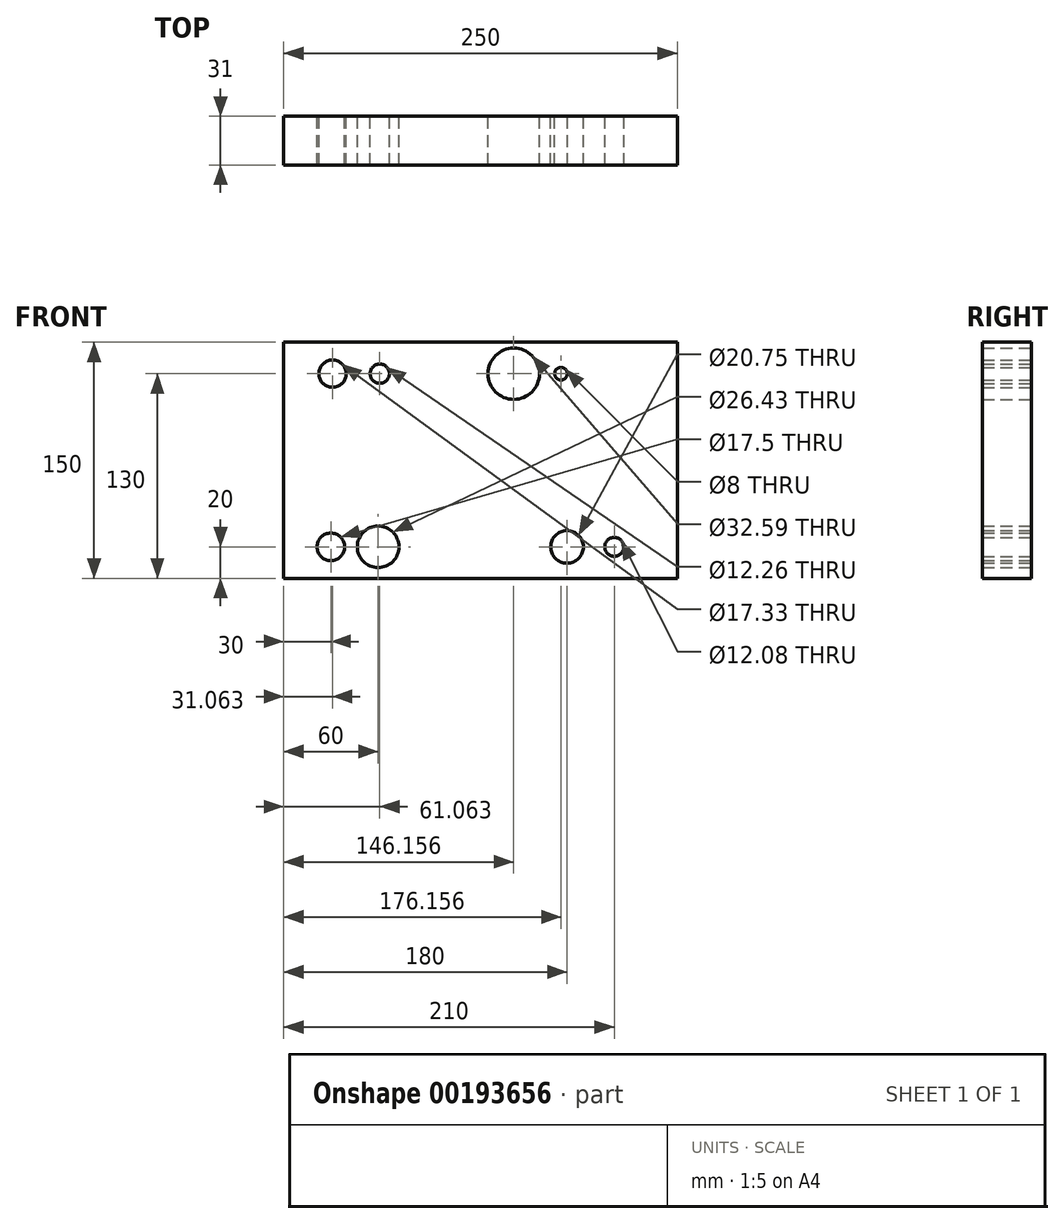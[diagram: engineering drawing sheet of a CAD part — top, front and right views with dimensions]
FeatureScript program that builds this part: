
annotation { "Feature Type Name" : "Feature", "Feature Type Description" : "" }
export const myFeature = defineFeature(function(context is Context, id is Id, definition is map)
    precondition{}
    {
        {
            var Q0;
            Q0=qCreatedBy(makeId("Front.planeOp"),FACE);
            var sketch = newSketch(context, id + "F0", { "sketchPlane" : qUnion([Q0])});
            skLineSegment(sketch, "E0.bottom", {"start": v(125, 75) * mm, "end": v(-125, 75) * mm});
            skLineSegment(sketch, "E0.top", {"start": v(125, -75) * mm, "end": v(-125, -75) * mm});
            skLineSegment(sketch, "E0.left", {"start": v(125, 75) * mm, "end": v(125, -75) * mm});
            skLineSegment(sketch, "E0.right", {"start": v(-125, 75) * mm, "end": v(-125, -75) * mm});
            skPoint(sketch, "E0.middle", {"position": v(0, 0) * mm});
            skCircle(sketch, "E1", {"center": v(-93.94, 55) * mm, "radius": 8.67 * mm});
            skCircle(sketch, "E2", {"center": v(-63.94, 55) * mm, "radius": 6.13 * mm});
            skCircle(sketch, "E3", {"center": v(21.16, 55) * mm, "radius": 16.3 * mm});
            skCircle(sketch, "E4", {"center": v(51.16, 55) * mm, "radius": 4 * mm});
            skCircle(sketch, "E5", {"center": v(-95, -55) * mm, "radius": 8.75 * mm});
            skCircle(sketch, "E6", {"center": v(-65, -55) * mm, "radius": 13.21 * mm});
            skCircle(sketch, "E7", {"center": v(55, -55) * mm, "radius": 10.37 * mm});
            skCircle(sketch, "E8", {"center": v(85, -55) * mm, "radius": 6.04 * mm});
            skSolve(sketch);
        }
        {
            var Q0;
            Q0=makeQuery(id+"F0.imprint","IMPRINT",FACE,{"disambiguationData":[TD([[makeQuery(id+"F0.imprint","IMPRINT",EDGE,{"derivedFrom":sQuery(id+"F0.wireOp",EDGE,"E0.bottom")}),1.0]])]});
            extrude(context, id + "F1", {"entities" : qUnion([Q0]), "depth" : 25 * mm});
        }
        {
            var Q0;
            Q0=makeQuery(id+"F1.opExtrude","CAP_FACE",FACE,{"disambiguationData":[OSD([sQuery(id+"F0.wireOp",EDGE,"E0.bottom"),sQuery(id+"F0.wireOp",EDGE,"E0.top"),sQuery(id+"F0.wireOp",EDGE,"E0.left"),sQuery(id+"F0.wireOp",EDGE,"E0.right"),sQuery(id+"F0.wireOp",EDGE,"E1"),sQuery(id+"F0.wireOp",EDGE,"E2"),sQuery(id+"F0.wireOp",EDGE,"E3"),sQuery(id+"F0.wireOp",EDGE,"E4"),sQuery(id+"F0.wireOp",EDGE,"E5"),sQuery(id+"F0.wireOp",EDGE,"E6"),sQuery(id+"F0.wireOp",EDGE,"E7"),sQuery(id+"F0.wireOp",EDGE,"E8")])],"isStart":false});
            extrude(context, id + "F2", {"entities" : qUnion([Q0]), "operationType" : NewBodyOperationType.ADD, "depth" : 6 * mm});
        }
    });
